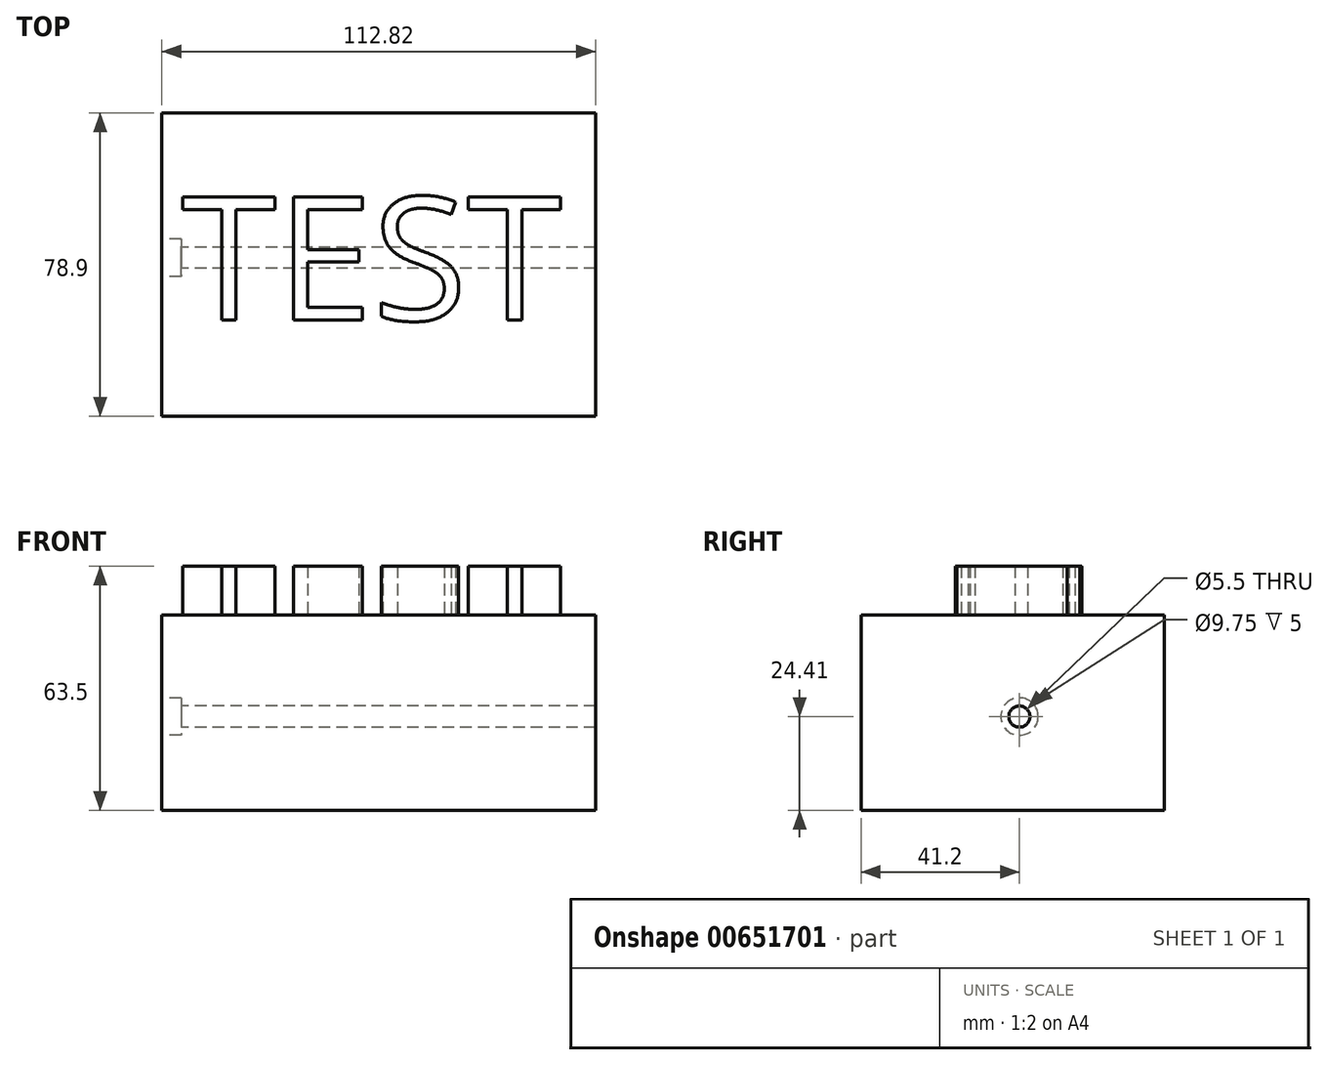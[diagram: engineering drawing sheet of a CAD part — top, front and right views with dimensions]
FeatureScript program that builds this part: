
annotation { "Feature Type Name" : "Feature", "Feature Type Description" : "" }
export const myFeature = defineFeature(function(context is Context, id is Id, definition is map)
    precondition{}
    {
        {
            var Q0;
            Q0=qCreatedBy(makeId("Top.planeOp"),FACE);
            var sketch = newSketch(context, id + "F0", { "sketchPlane" : qUnion([Q0])});
            skLineSegment(sketch, "E0.bottom", {"start": v(-50.42, 37.7) * mm, "end": v(62.4, 37.7) * mm});
            skLineSegment(sketch, "E0.top", {"start": v(-50.42, -41.2) * mm, "end": v(62.4, -41.2) * mm});
            skLineSegment(sketch, "E0.left", {"start": v(-50.42, 37.7) * mm, "end": v(-50.42, -41.2) * mm});
            skLineSegment(sketch, "E0.right", {"start": v(62.4, 37.7) * mm, "end": v(62.4, -41.2) * mm});
            skSolve(sketch);
        }
        {
            var Q0;
            Q0=makeQuery(id+"F0.imprint","IMPRINT",FACE,{"disambiguationData":[TD([[makeQuery(id+"F0.imprint","IMPRINT",EDGE,{"derivedFrom":sQuery(id+"F0.wireOp",EDGE,"E0.bottom")}),-1.0]])]});
            extrude(context, id + "F1", {"entities" : qUnion([Q0]), "depth" : 50.8 * mm, "offsetDistance" : 25.4 * mm});
        }
        {
            var Q0;
            Q0=makeQuery(id+"F1.opExtrude","CAP_FACE",FACE,{"disambiguationData":[OSD([sQuery(id+"F0.wireOp",EDGE,"E0.bottom"),sQuery(id+"F0.wireOp",EDGE,"E0.top"),sQuery(id+"F0.wireOp",EDGE,"E0.left"),sQuery(id+"F0.wireOp",EDGE,"E0.right")])],"isStart":false});
            var sketch = newSketch(context, id + "F2", { "sketchPlane" : qUnion([Q0])});
            skText(sketch, "E1", { "text": "TEST", "fontName": "OpenSans-Regular.ttf"});
            const initialGuessF2  = {"E1": [-0.04534, -0.01622, 1, 0, 0.03227]};
            skSetInitialGuess(sketch, initialGuessF2);
            skSolve(sketch);
        }
        {
            var Q0;
            Q0 = qSketchRegion(id + "F2", true);
            extrude(context, id + "F3", {"entities" : qUnion([Q0]), "operationType" : NewBodyOperationType.ADD, "depth" : 12.7 * mm, "offsetDistance" : 25.4 * mm});
        }
        {
            var Q0;
            Q0=makeQuery(id+"F1.opExtrude","SWEPT_FACE",FACE,{"disambiguationData":[OSD([sQuery(id+"F0.wireOp",EDGE,"E0.left")])]});
            var sketch = newSketch(context, id + "F4", { "sketchPlane" : qUnion([Q0])});
            skCircle(sketch, "E2", {"center": v(0, 24.41) * mm, "radius": 10.4 * mm});
            skSolve(sketch);
        }
        {
            var Q0;
            Q0=sQuery(id+"F4.wireOp",VERTEX,"E2.center");
            var Q1;
            Q1=makeQuery(id+"F1.opExtrude","SWEPT_BODY",BODY,{"disambiguationData":[OSD([sQuery(id+"F0.wireOp",EDGE,"E0.bottom"),sQuery(id+"F0.wireOp",EDGE,"E0.top"),sQuery(id+"F0.wireOp",EDGE,"E0.left"),sQuery(id+"F0.wireOp",EDGE,"E0.right")])]});
            hole(context, id + "F5", {"style" : HoleStyle.C_BORE, "endStyle" : HoleEndStyle.THROUGH, "standardTappedOrClearance" : lookupTablePath({ "standard" : "ISO", "fit" : "Normal", "size" : "M5", "type" : "Clearance" }), "standardBlindInLast" : lookupTablePath({ "fit" : "Standard", "standard" : "ISO", "size" : "M5", "type" : "Clearance" }), "holeDiameter" : 5.5 * mm, "cBoreDiameter" : 9.75 * mm, "cBoreDepth" : 5 * mm, "majorDiameter" : 6.35 * mm, "isTappedThrough" : true, "tappedDepth" : 12.7 * mm, "tapClearance" : 3, "locations" : qUnion([Q0]), "scope" : qUnion([Q1])});
        }
    });
